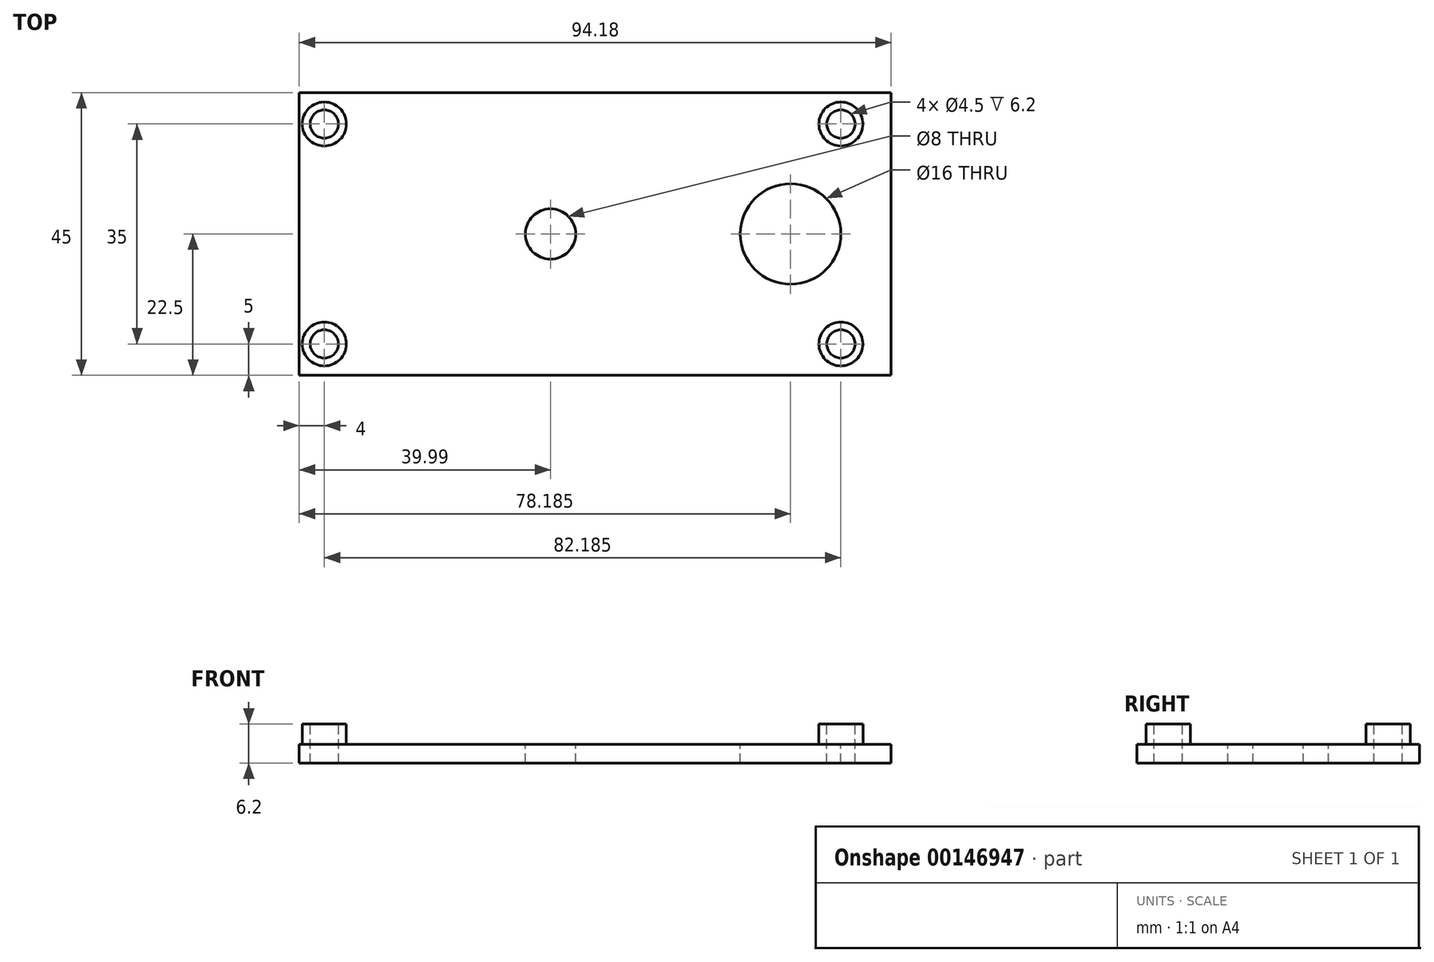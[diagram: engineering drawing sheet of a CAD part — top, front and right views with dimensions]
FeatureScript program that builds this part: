
annotation { "Feature Type Name" : "Feature", "Feature Type Description" : "" }
export const myFeature = defineFeature(function(context is Context, id is Id, definition is map)
    precondition{}
    {
        {
            var Q0;
            Q0=qCreatedBy(makeId("Top.planeOp"),FACE);
            var sketch = newSketch(context, id + "F0", { "sketchPlane" : qUnion([Q0])});
            skLineSegment(sketch, "E0", {"start": v(0, 0) * mm, "end": v(-63.98, 0) * mm, "construction": true});
            skLineSegment(sketch, "E1", {"start": v(0, 0) * mm, "end": v(12.4, 0) * mm, "construction": true});
            skLineSegment(sketch, "E2", {"start": v(12.4, 0) * mm, "end": v(14.2, 0) * mm, "construction": true});
            skLineSegment(sketch, "E3", {"start": v(14.2, 17.5) * mm, "end": v(14.2, -17.5) * mm, "construction": true});
            skCircle(sketch, "E4", {"center": v(6.2, 0) * mm, "radius": 6.2 * mm, "construction": true});
            skCircle(sketch, "E5", {"center": v(-31.99, 0) * mm, "radius": 31.99 * mm, "construction": true});
            skCircle(sketch, "E6", {"center": v(14.2, 17.5) * mm, "radius": 2.25 * mm});
            skCircle(sketch, "E7", {"center": v(14.2, -17.5) * mm, "radius": 2.25 * mm});
            skCircle(sketch, "E8", {"center": v(6.2, 0) * mm, "radius": 5 * mm});
            skCircle(sketch, "E9", {"center": v(-31.99, 0) * mm, "radius": 4 * mm});
            skCircle(sketch, "E10", {"center": v(6.2, 0) * mm, "radius": 8 * mm});
            skLineSegment(sketch, "E11", {"start": v(14.2, 0) * mm, "end": v(22.2, 0) * mm, "construction": true});
            skLineSegment(sketch, "E12", {"start": v(22.2, 22.5) * mm, "end": v(22.2, -22.5) * mm, "construction": true});
            skLineSegment(sketch, "E13.bottom", {"start": v(22.2, 22.5) * mm, "end": v(-1.8, 22.5) * mm});
            skLineSegment(sketch, "E13.top", {"start": v(22.2, -22.5) * mm, "end": v(-1.8, -22.5) * mm});
            skLineSegment(sketch, "E13.left", {"start": v(22.2, 22.5) * mm, "end": v(22.2, -22.5) * mm});
            skLineSegment(sketch, "E13.right", {"start": v(-1.8, 22.5) * mm, "end": v(-1.8, -22.5) * mm});
            skLineSegment(sketch, "E14.bottom", {"start": v(-1.8, 22.5) * mm, "end": v(-71.98, 22.5) * mm});
            skLineSegment(sketch, "E14.top", {"start": v(-1.8, -22.5) * mm, "end": v(-71.98, -22.5) * mm});
            skLineSegment(sketch, "E14.right", {"start": v(-71.98, 22.5) * mm, "end": v(-71.98, -22.5) * mm});
            skLineSegment(sketch, "E15", {"start": v(-63.98, 0) * mm, "end": v(-71.98, 0) * mm, "construction": true});
            skLineSegment(sketch, "E16", {"start": v(-67.98, 17.5) * mm, "end": v(-67.98, -17.5) * mm, "construction": true});
            skPoint(sketch, "E16.startSnap0", {"position": v(-67.98, 0) * mm});
            skCircle(sketch, "E17", {"center": v(-67.98, 17.5) * mm, "radius": 2.25 * mm});
            skCircle(sketch, "E18", {"center": v(-67.98, -17.5) * mm, "radius": 2.25 * mm});
            skCircle(sketch, "E19", {"center": v(-67.98, 17.5) * mm, "radius": 3.5 * mm});
            skCircle(sketch, "E20", {"center": v(-67.98, -17.5) * mm, "radius": 3.5 * mm});
            skCircle(sketch, "E21", {"center": v(14.2, -17.5) * mm, "radius": 3.5 * mm});
            skCircle(sketch, "E22", {"center": v(14.2, 17.5) * mm, "radius": 3.5 * mm});
            skSolve(sketch);
        }
        {
            var Q0;
            Q0=makeQuery(id+"F0.imprint","IMPRINT",FACE,{"disambiguationData":[TD([[makeQuery(id+"F0.imprint","IMPRINT",EDGE,{"derivedFrom":sQuery(id+"F0.wireOp",EDGE,"E9")}),-1.0]])]});
            var Q1;
            {var subQ2=sQuery(id+"F0.wireOp",EDGE,"E10");Q1=makeQuery(id+"F0.imprint","IMPRINT",FACE,{"disambiguationData":[TD([[makeQuery(id+"F0.imprint","IMPRINT",EDGE,{"derivedFrom":subQ2}),-1.0]])]});}
            var Q2;
            Q2=makeQuery(id+"F0.imprint","IMPRINT",FACE,{"disambiguationData":[TD([[makeQuery(id+"F0.imprint","IMPRINT",EDGE,{"derivedFrom":sQuery(id+"F0.wireOp",EDGE,"E17")}),-1.0]])]});
            var Q3;
            Q3=makeQuery(id+"F0.imprint","IMPRINT",FACE,{"disambiguationData":[TD([[makeQuery(id+"F0.imprint","IMPRINT",EDGE,{"derivedFrom":sQuery(id+"F0.wireOp",EDGE,"E18")}),-1.0]])]});
            var Q4;
            Q4=makeQuery(id+"F0.imprint","IMPRINT",FACE,{"disambiguationData":[TD([[makeQuery(id+"F0.imprint","IMPRINT",EDGE,{"derivedFrom":sQuery(id+"F0.wireOp",EDGE,"E7")}),-1.0]])]});
            var Q5;
            Q5=makeQuery(id+"F0.imprint","IMPRINT",FACE,{"disambiguationData":[TD([[makeQuery(id+"F0.imprint","IMPRINT",EDGE,{"derivedFrom":sQuery(id+"F0.wireOp",EDGE,"E6")}),-1.0]])]});
            extrude(context, id + "F1", {"entities" : qUnion([Q0, Q1, Q2, Q3, Q4, Q5]), "oppositeDirection" : true, "depth" : 3 * mm});
        }
        {
            var Q0;
            Q0=makeQuery(id+"F0.imprint","IMPRINT",FACE,{"disambiguationData":[TD([[makeQuery(id+"F0.imprint","IMPRINT",EDGE,{"derivedFrom":sQuery(id+"F0.wireOp",EDGE,"E17")}),-1.0]])]});
            var Q1;
            Q1=makeQuery(id+"F0.imprint","IMPRINT",FACE,{"disambiguationData":[TD([[makeQuery(id+"F0.imprint","IMPRINT",EDGE,{"derivedFrom":sQuery(id+"F0.wireOp",EDGE,"E18")}),-1.0]])]});
            var Q2;
            Q2=makeQuery(id+"F0.imprint","IMPRINT",FACE,{"disambiguationData":[TD([[makeQuery(id+"F0.imprint","IMPRINT",EDGE,{"derivedFrom":sQuery(id+"F0.wireOp",EDGE,"E7")}),-1.0]])]});
            var Q3;
            Q3=makeQuery(id+"F0.imprint","IMPRINT",FACE,{"disambiguationData":[TD([[makeQuery(id+"F0.imprint","IMPRINT",EDGE,{"derivedFrom":sQuery(id+"F0.wireOp",EDGE,"E6")}),-1.0]])]});
            extrude(context, id + "F2", {"entities" : qUnion([Q0, Q1, Q2, Q3]), "operationType" : NewBodyOperationType.ADD, "depth" : 3.2 * mm});
        }
    });
